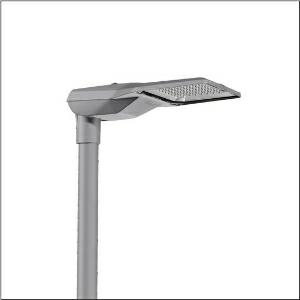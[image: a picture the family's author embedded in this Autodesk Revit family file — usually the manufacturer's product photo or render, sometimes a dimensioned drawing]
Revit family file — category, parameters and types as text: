
# Revit family: streetlight_sl_21_midi___pl52_5xe3h43s08mb_aca6
name_source: partatom
category: Lighting Fixtures
units: mm (PartAtom-declared; Revit-internal decimal feet)

## family parameters
Cut with Voids When Loaded = No
Host = Face
Light Source = No
Part Type = Normal
Room Calculation Point = No
Round Connector Dimension = Use Diameter
Shared = No

## types (1)
- --- (1 x LED, 19830 lm, 147 W, 4000K)
    Apparent Load = 147 VA
    CIE Flux Codes = 27 59 98 100 100
    Color Rendering = 70
    Color Temperature = 4000K
    Default Elevation = 1800 mm
    Description = Streetlight SL 21 midi, mast luminaire, primary light control with lens, of PMMA, primary optical cover: cover, of toughened safety glass, transparent, light distribution: PL52, light emission: direct distribution, primary light characteristic: asymmetric, installation type: side-entry, post-top, LED, High Power LED, rated luminous flux: 19.830lm, luminous efficacy: 135lm/W, light colour: 740, colour temperature: 4000K, control gear: D4i, control: overheat protection, constant luminous flux control, time-dependent luminous flux control, flexible luminous flux parameterisation, pre-setting: logarithmic dimming characteristic, mains connection: 230..240V, AC, 50/60Hz, start of lifetime: 147W, end of service life: 155W, reduction: 65W, luminaire housing, of diecast aluminium, powder-coated, SITECO metallic grey (DB 702S), corrosivity category C5 high according to DIN EN ISO 12944, please order mast flange separately, inclination adjustable: 0°, 5°, 10°, 15°, sealing non-destructively replaceable, multi-level sealing system, length: 644mm, width: 335mm, height: 110mm, mast flange for spigot size: 42mm (side-entry): 5XC10008XM4, 60/48mm (side-entry/post-top): 5XC10108XM2, 76/60mm (side-entry/post-top): 5XC10108XM1, mounting height: 4..8m, Smart Interface above, protection rating (complete): IP66, insulation class (complete): insulation class II (safety insulation), certification: CE, ENEC, ENEC+, VDE, impact resistance: IK10, permissible operating ambient temperature for outdoor applications: -40..+50°C, standard-compliant lighting for roads and squares, packaging unit: 1 piece

Light Distribution: PL52
    Height = 111 mm
    Lamp = 1 x LED
    Lamp Light Flux = 19830 lm
    Lamp Power = 147 W
    Lamp count = 1
    Length = 644 mm
    Luminous efficacy = 135 lm/W
    Manufacturer = Siteco
    ModVariant = No
    Model = 5XE3H43S08MB
    Number of Poles = 1
    OnlyDefault = Yes
    Power Factor = 1
    Product Name = Streetlight SL 21 midi | PL52
    Product group = mast luminaire | pylon top
    ProductGroupID = 6100
    Protection Class = Protection class II
    Protection Degree = IP 66
    RLX_Detail_Level = 1
    RLX_Emergency_Light_Flux = 0 lm
    RLX_Emergency_Type = 0
    RLX_Emergency_Type_DB = No
    RlxData = <blob elided: 36469 chars, md5=6058cc00>
    Socket = socket
    Standby Power = 0 W
    System Light Flux = 19830 lm
    System Power = 147 W
    Type Comments = factory setting: luminous flux: 100 % | dim-lin: 254 | 750 mA
    Type Image = l_1004302.jpg
    URL = http://relux.com
    VarID = @adj_188091
    Voltage = 0 V
    Weight = 0.00 kg
    Width = 336 mm

## geometry (parser evidence)
native form markers: Blend x4, Sweep x9
no freeform markers — native parametric forms only
